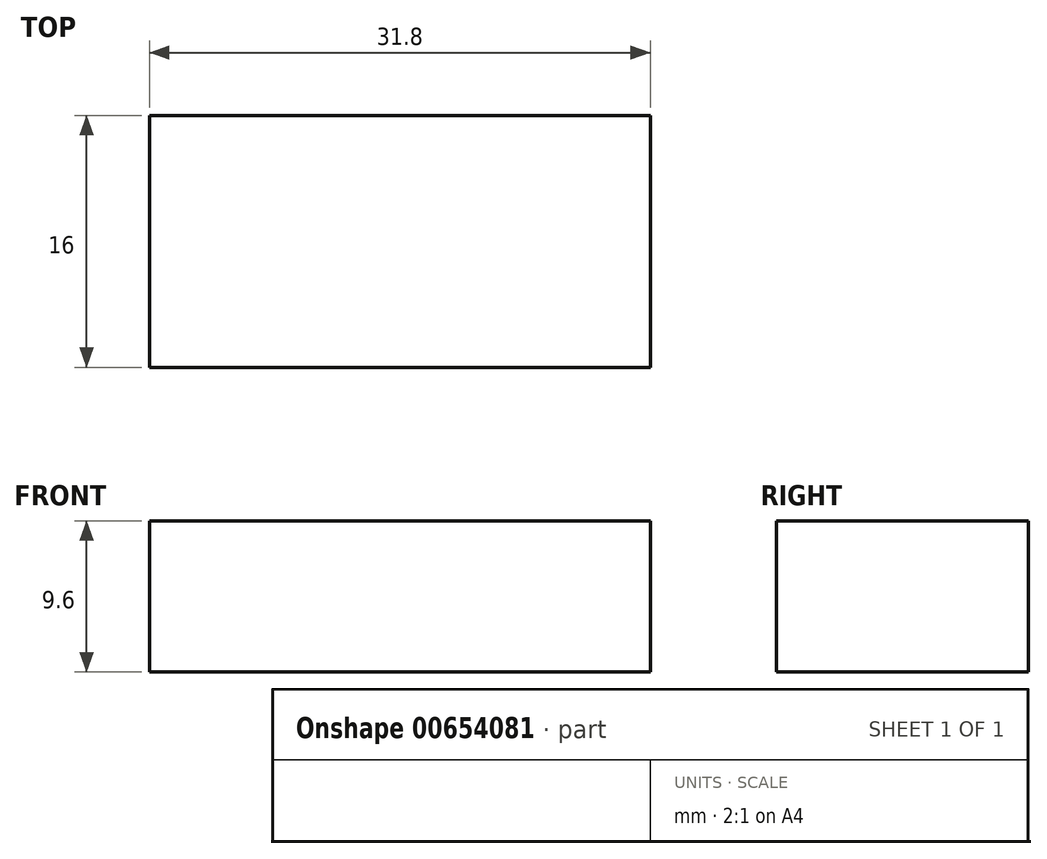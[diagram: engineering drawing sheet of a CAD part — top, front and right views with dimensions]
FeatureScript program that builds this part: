
annotation { "Feature Type Name" : "Feature", "Feature Type Description" : "" }
export const myFeature = defineFeature(function(context is Context, id is Id, definition is map)
    precondition{}
    {
        {
            var Q0;
            Q0=qCreatedBy(makeId("Top.planeOp"),FACE);
            var sketch = newSketch(context, id + "F0", { "sketchPlane" : qUnion([Q0])});
            skLineSegment(sketch, "E0.bottom", {"start": v(0, 0) * mm, "end": v(-31.8, 0) * mm});
            skLineSegment(sketch, "E0.top", {"start": v(0, 16) * mm, "end": v(-31.8, 16) * mm});
            skLineSegment(sketch, "E0.left", {"start": v(0, 0) * mm, "end": v(0, 16) * mm});
            skLineSegment(sketch, "E0.right", {"start": v(-31.8, 0) * mm, "end": v(-31.8, 16) * mm});
            skSolve(sketch);
        }
        {
            var Q0;
            Q0=makeQuery(id+"F0.imprint","IMPRINT",FACE,{"disambiguationData":[TD([[makeQuery(id+"F0.imprint","IMPRINT",EDGE,{"derivedFrom":sQuery(id+"F0.wireOp",EDGE,"E0.bottom")}),-1.0]])]});
            extrude(context, id + "F1", {"entities" : qUnion([Q0]), "depth" : 9.6 * mm, "offsetDistance" : 25.4 * mm});
        }
    });
